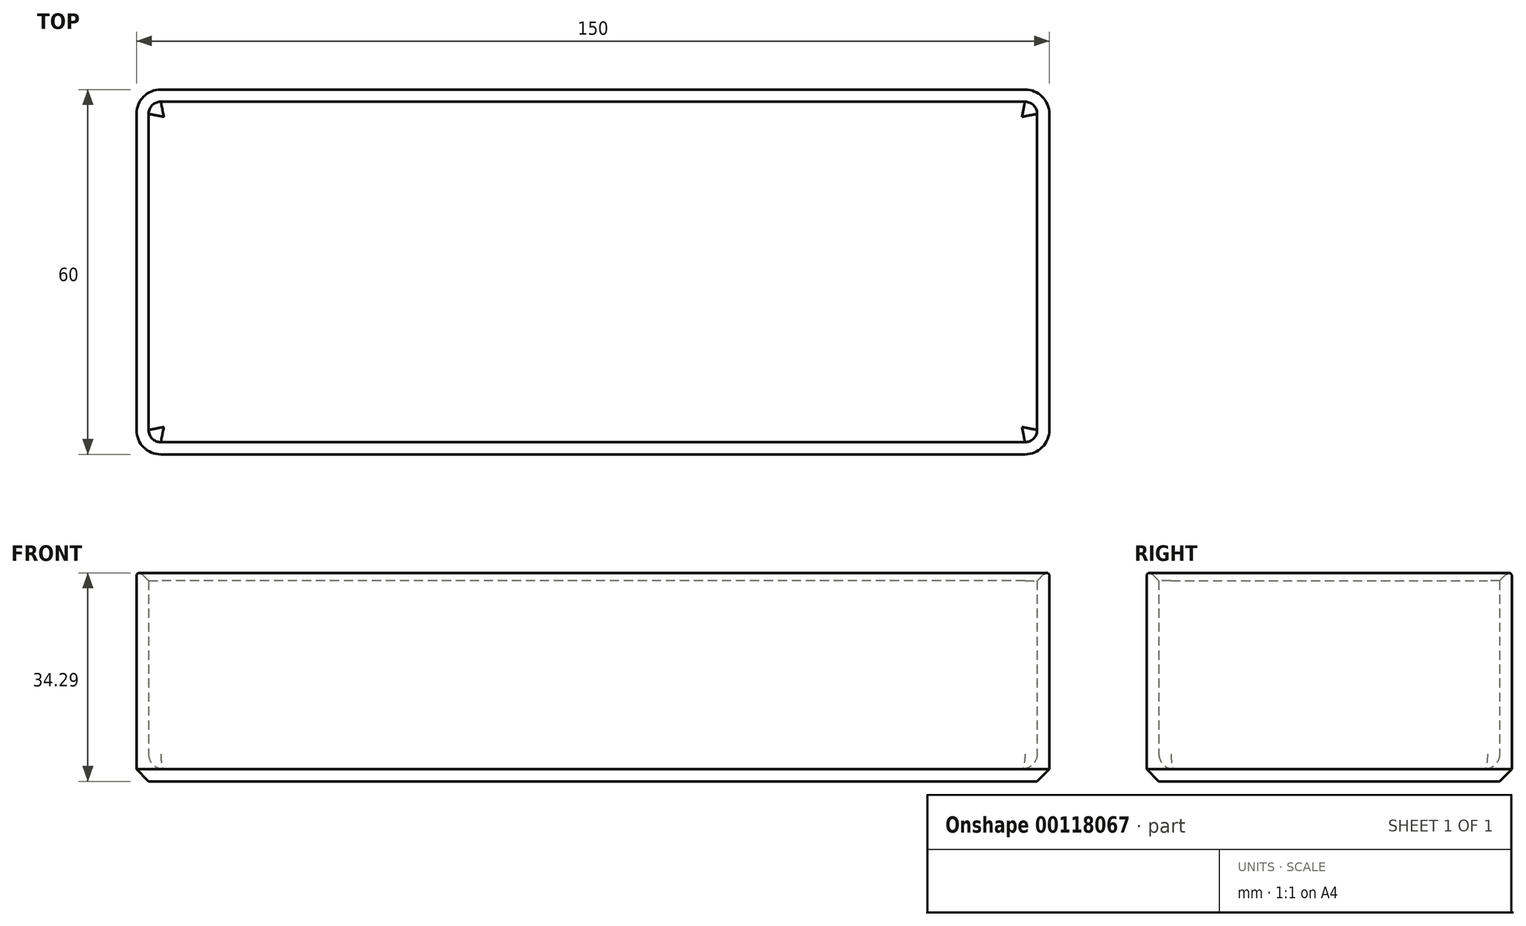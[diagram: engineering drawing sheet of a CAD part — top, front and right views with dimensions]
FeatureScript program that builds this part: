
annotation { "Feature Type Name" : "Feature", "Feature Type Description" : "" }
export const myFeature = defineFeature(function(context is Context, id is Id, definition is map)
    precondition{}
    {
        {
            var Q0;
            Q0=qCreatedBy(makeId("Top.planeOp"),FACE);
            var sketch = newSketch(context, id + "F0", { "sketchPlane" : qUnion([Q0])});
            skLineSegment(sketch, "E0.bottom", {"start": v(75, 30) * mm, "end": v(-75, 30) * mm});
            skLineSegment(sketch, "E0.top", {"start": v(75, -30) * mm, "end": v(-75, -30) * mm});
            skLineSegment(sketch, "E0.left", {"start": v(75, 30) * mm, "end": v(75, -30) * mm});
            skLineSegment(sketch, "E0.right", {"start": v(-75, 30) * mm, "end": v(-75, -30) * mm});
            skPoint(sketch, "E0.middle", {"position": v(0, 0) * mm});
            skSolve(sketch);
        }
        {
            var Q0;
            Q0=makeQuery(id+"F0.imprint","IMPRINT",FACE,{"disambiguationData":[TD([[makeQuery(id+"F0.imprint","IMPRINT",EDGE,{"derivedFrom":sQuery(id+"F0.wireOp",EDGE,"E0.bottom")}),1.0]])]});
            extrude(context, id + "F1", {"entities" : qUnion([Q0]), "depth" : 35 * mm});
        }
        {
            var Q0;
            Q0=makeQuery(id+"F1.opExtrude","CAP_FACE",FACE,{"disambiguationData":[OSD([sQuery(id+"F0.wireOp",EDGE,"E0.bottom"),sQuery(id+"F0.wireOp",EDGE,"E0.top"),sQuery(id+"F0.wireOp",EDGE,"E0.left"),sQuery(id+"F0.wireOp",EDGE,"E0.right")])],"isStart":false});
            shell(context, id + "F2", {"entities" : qUnion([Q0]), "thickness" : 2 * mm});
        }
        {
            var Q0;
            Q0=makeQuery(id+"F2.opShell","OFFSET_EDGE",EDGE,{"disambiguationData":[OSD([sQuery(id+"F0.wireOp",EDGE,"E0.bottom"),sQuery(id+"F0.wireOp",EDGE,"E0.left")])]});
            var Q1;
            Q1=makeQuery(id+"F2.opShell","OFFSET_EDGE",EDGE,{"disambiguationData":[OSD([sQuery(id+"F0.wireOp",EDGE,"E0.bottom"),sQuery(id+"F0.wireOp",EDGE,"E0.right")])]});
            var Q2;
            Q2=makeQuery(id+"F2.opShell","OFFSET_EDGE",EDGE,{"disambiguationData":[OSD([sQuery(id+"F0.wireOp",EDGE,"E0.top"),sQuery(id+"F0.wireOp",EDGE,"E0.left")])]});
            var Q3;
            Q3=makeQuery(id+"F2.opShell","OFFSET_EDGE",EDGE,{"disambiguationData":[OSD([sQuery(id+"F0.wireOp",EDGE,"E0.top"),sQuery(id+"F0.wireOp",EDGE,"E0.right")])]});
            fillet(context, id + "F3", {"entities" : qUnion([Q0, Q1, Q2, Q3]), "radius" : 2 * mm, "tangentPropagation" : true, "allowEdgeOverflow" : false});
        }
        {
            var Q0;
            Q0=makeQuery(id+"F1.opExtrude","SWEPT_EDGE",EDGE,{"disambiguationData":[OSD([sQuery(id+"F0.wireOp",EDGE,"E0.top"),sQuery(id+"F0.wireOp",EDGE,"E0.right")])]});
            var Q1;
            Q1=makeQuery(id+"F1.opExtrude","SWEPT_EDGE",EDGE,{"disambiguationData":[OSD([sQuery(id+"F0.wireOp",EDGE,"E0.top"),sQuery(id+"F0.wireOp",EDGE,"E0.left")])]});
            var Q2;
            Q2=makeQuery(id+"F1.opExtrude","SWEPT_EDGE",EDGE,{"disambiguationData":[OSD([sQuery(id+"F0.wireOp",EDGE,"E0.bottom"),sQuery(id+"F0.wireOp",EDGE,"E0.left")])]});
            var Q3;
            Q3=makeQuery(id+"F1.opExtrude","SWEPT_EDGE",EDGE,{"disambiguationData":[OSD([sQuery(id+"F0.wireOp",EDGE,"E0.bottom"),sQuery(id+"F0.wireOp",EDGE,"E0.right")])]});
            fillet(context, id + "F4", {"entities" : qUnion([Q0, Q1, Q2, Q3]), "radius" : 4 * mm, "tangentPropagation" : true, "allowEdgeOverflow" : false});
        }
        {
            var Q0;
            {var subQ0=sQuery(id+"F0.wireOp",EDGE,"E0.bottom");Q0=makeQuery(id+"F2.opShell","OFFSET_EDGE",EDGE,{"disambiguationData":[OSD([subQ0]),TDD([makeQuery(id+"F1.opExtrude","CAP_EDGE",EDGE,{"disambiguationData":[OSD([subQ0])],"isStart":true})])]});}
            fillet(context, id + "F5", {"entities" : qUnion([Q0]), "radius" : 2.5 * mm, "tangentPropagation" : true, "allowEdgeOverflow" : false});
        }
        {
            var Q0;
            Q0=makeQuery(id+"F1.opExtrude","CAP_EDGE",EDGE,{"disambiguationData":[OSD([sQuery(id+"F0.wireOp",EDGE,"E0.bottom")])],"isStart":true});
            chamfer(context, id + "F6", {"entities" : qUnion([Q0]), "width" : 2 * mm, "tangentPropagation" : true});
        }
        {
            var Q0;
            {var subQ0=sQuery(id+"F0.wireOp",EDGE,"E0.left");Q0=makeQuery(id+"F2.opShell","OFFSET_EDGE",EDGE,{"disambiguationData":[OSD([subQ0]),TDD([makeQuery(id+"F1.opExtrude","CAP_EDGE",EDGE,{"disambiguationData":[OSD([subQ0])],"isStart":false})])]});}
            chamfer(context, id + "F7", {"entities" : qUnion([Q0]), "width" : 2 * mm, "tangentPropagation" : true});
        }
        {
            var Q0;
            {var subQ0=sQuery(id+"F0.wireOp",EDGE,"E0.top");Q0=makeQuery(id+"F7.opChamfer","BLEND_EDGE",EDGE,{"blendedFrom":[makeQuery(id+"F2.opShell","OFFSET_EDGE",EDGE,{"disambiguationData":[OSD([subQ0]),TDD([makeQuery(id+"F1.opExtrude","CAP_EDGE",EDGE,{"disambiguationData":[OSD([subQ0])],"isStart":false})])]}),makeQuery(id+"F1.opExtrude","SWEPT_FACE",FACE,{"disambiguationData":[OSD([subQ0])]})],"blendedInto":[makeQuery(id+"F1.opExtrude","SWEPT_FACE",FACE,{"disambiguationData":[OSD([subQ0])]})]});}
            fillet(context, id + "F8", {"entities" : qUnion([Q0]), "radius" : 0.5 * mm, "tangentPropagation" : true, "allowEdgeOverflow" : false});
        }
    });
